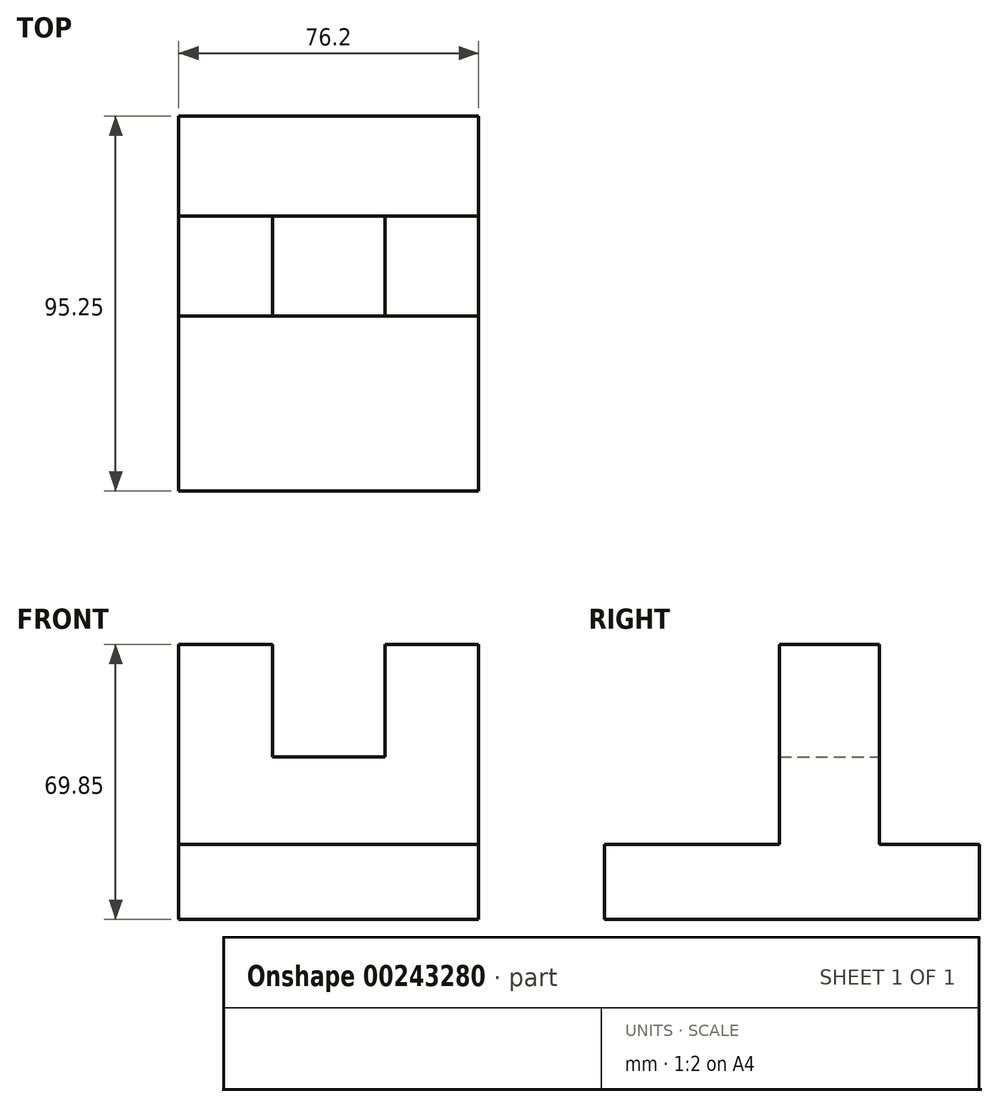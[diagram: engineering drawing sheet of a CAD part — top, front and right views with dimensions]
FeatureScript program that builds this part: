
annotation { "Feature Type Name" : "Feature", "Feature Type Description" : "" }
export const myFeature = defineFeature(function(context is Context, id is Id, definition is map)
    precondition{}
    {
        {
            var Q0;
            Q0=qCreatedBy(makeId("Right.planeOp"),FACE);
            var sketch = newSketch(context, id + "F0", { "sketchPlane" : qUnion([Q0])});
            skLineSegment(sketch, "E0", {"start": v(0, 0) * mm, "end": v(43.67, 0) * mm});
            skLineSegment(sketch, "E1", {"start": v(43.67, 0) * mm, "end": v(43.67, 19.05) * mm});
            skLineSegment(sketch, "E2", {"start": v(43.67, 19.05) * mm, "end": v(18.27, 19.05) * mm});
            skLineSegment(sketch, "E3", {"start": v(18.27, 19.05) * mm, "end": v(18.27, 69.85) * mm});
            skLineSegment(sketch, "E4", {"start": v(18.27, 69.85) * mm, "end": v(-7.13, 69.85) * mm});
            skLineSegment(sketch, "E5", {"start": v(-7.13, 69.85) * mm, "end": v(-7.13, 19.05) * mm});
            skLineSegment(sketch, "E6", {"start": v(-7.13, 19.05) * mm, "end": v(-51.58, 19.05) * mm});
            skLineSegment(sketch, "E7", {"start": v(-51.58, 19.05) * mm, "end": v(-51.58, 0) * mm});
            skLineSegment(sketch, "E8", {"start": v(-51.58, 0) * mm, "end": v(0, 0) * mm});
            skSolve(sketch);
        }
        {
            var Q0;
            Q0=makeQuery(id+"F0.imprint","IMPRINT",FACE,{"disambiguationData":[TD([[makeQuery(id+"F0.imprint","IMPRINT",EDGE,{"derivedFrom":sQuery(id+"F0.wireOp",EDGE,"E0")}),1.0]])]});
            extrude(context, id + "F1", {"entities" : qUnion([Q0]), "depth" : 76.2 * mm});
        }
        {
            var Q0;
            Q0=makeQuery(id+"F1.opExtrude","SWEPT_FACE",FACE,{"disambiguationData":[OSD([sQuery(id+"F0.wireOp",EDGE,"E3")])]});
            var sketch = newSketch(context, id + "F2", { "sketchPlane" : qUnion([Q0])});
            skLineSegment(sketch, "E9", {"start": v(-52.37, 69.85) * mm, "end": v(-52.37, 41.27) * mm});
            skLineSegment(sketch, "E10", {"start": v(-52.37, 41.27) * mm, "end": v(-23.8, 41.27) * mm});
            skLineSegment(sketch, "E11", {"start": v(-23.8, 41.27) * mm, "end": v(-23.8, 69.85) * mm});
            skLineSegment(sketch, "E12", {"start": v(-23.8, 69.85) * mm, "end": v(-52.37, 69.85) * mm});
            skSolve(sketch);
        }
        {
            var Q0;
            Q0=makeQuery(id+"F2.imprint","IMPRINT",FACE,{"disambiguationData":[TD([[makeQuery(id+"F2.imprint","IMPRINT",EDGE,{"derivedFrom":sQuery(id+"F2.wireOp",EDGE,"E9")}),1.0]])]});
            extrude(context, id + "F3", {"entities" : qUnion([Q0]), "operationType" : NewBodyOperationType.REMOVE, "oppositeDirection" : true, "depth" : 25.4 * mm});
        }
    });
